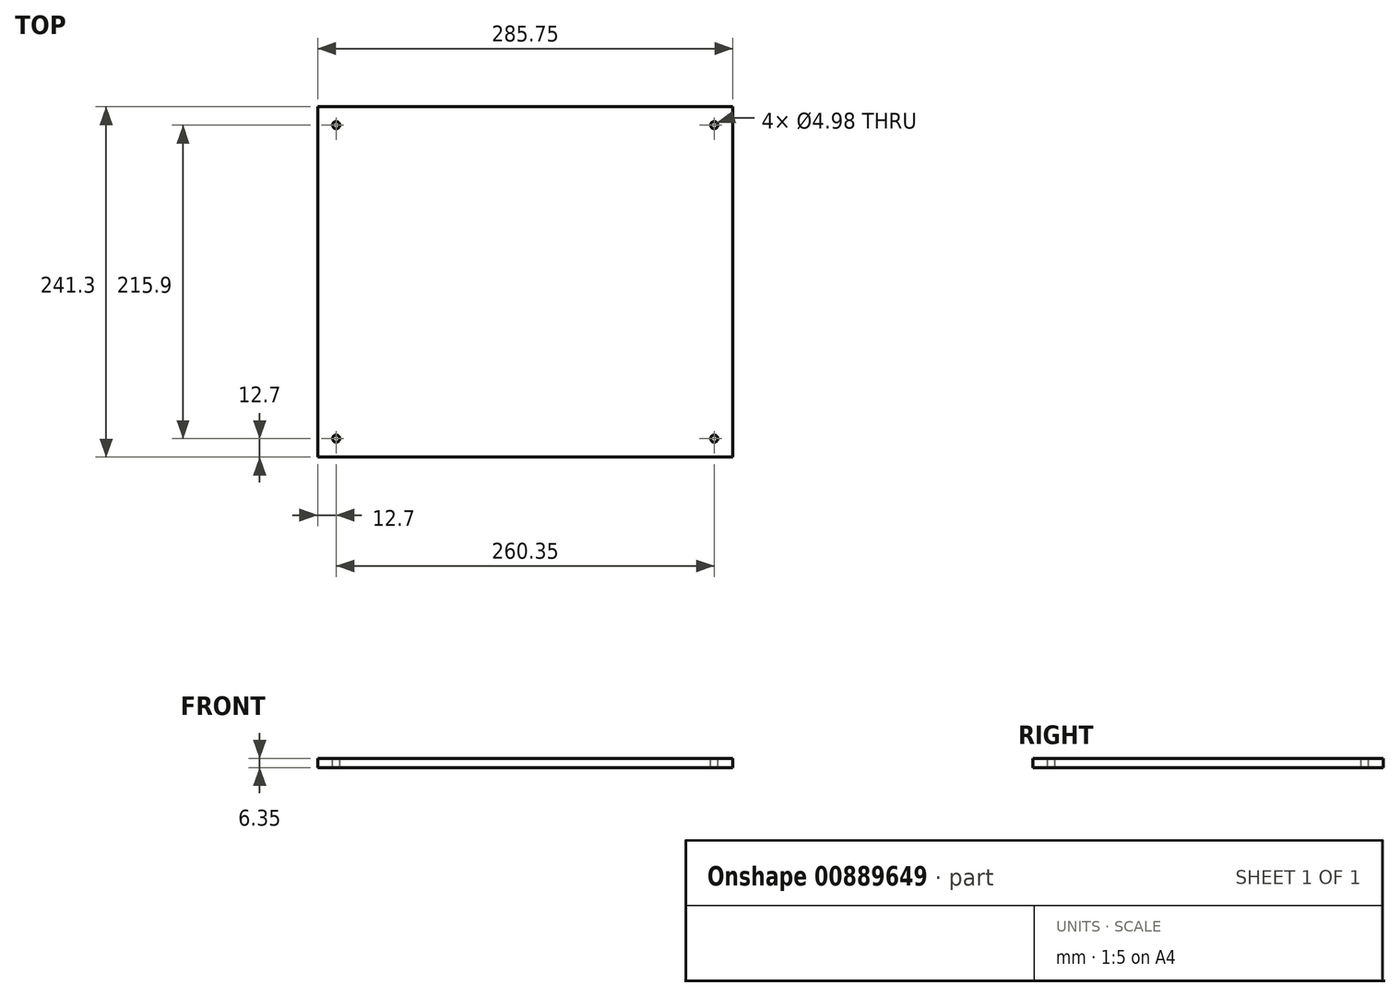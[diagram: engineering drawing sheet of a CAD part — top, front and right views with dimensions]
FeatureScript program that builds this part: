
annotation { "Feature Type Name" : "Feature", "Feature Type Description" : "" }
export const myFeature = defineFeature(function(context is Context, id is Id, definition is map)
    precondition{}
    {
        {
            var Q0;
            Q0=qCreatedBy(makeId("Top.planeOp"),FACE);
            var sketch = newSketch(context, id + "F0", { "sketchPlane" : qUnion([Q0])});
            skLineSegment(sketch, "E0.bottom", {"start": v(0, 0) * mm, "end": v(285.75, 0) * mm});
            skLineSegment(sketch, "E0.top", {"start": v(0, 241.3) * mm, "end": v(285.75, 241.3) * mm});
            skLineSegment(sketch, "E0.left", {"start": v(0, 0) * mm, "end": v(0, 241.3) * mm});
            skLineSegment(sketch, "E0.right", {"start": v(285.75, 0) * mm, "end": v(285.75, 241.3) * mm});
            skSolve(sketch);
        }
        {
            var Q0;
            Q0 = qSketchRegion(id + "F0", true);
            extrude(context, id + "F1", {"entities" : qUnion([Q0]), "depth" : 6.35 * mm, "offsetDistance" : 25.4 * mm});
        }
        {
            var Q0;
            Q0=makeQuery(id+"F1.opExtrude","CAP_FACE",FACE,{"disambiguationData":[OSD([sQuery(id+"F0.wireOp",EDGE,"E0.bottom"),sQuery(id+"F0.wireOp",EDGE,"E0.top"),sQuery(id+"F0.wireOp",EDGE,"E0.left"),sQuery(id+"F0.wireOp",EDGE,"E0.right")])],"isStart":false});
            var sketch = newSketch(context, id + "F2", { "sketchPlane" : qUnion([Q0])});
            skCircle(sketch, "E1", {"center": v(12.7, 12.7) * mm, "radius": 2.49 * mm});
            skCircle(sketch, "E2", {"center": v(12.7, 228.6) * mm, "radius": 2.49 * mm});
            skCircle(sketch, "E3", {"center": v(273.05, 228.6) * mm, "radius": 2.49 * mm});
            skCircle(sketch, "E4", {"center": v(273.05, 12.7) * mm, "radius": 2.49 * mm});
            skSolve(sketch);
        }
        {
            var Q0;
            Q0 = qSketchRegion(id + "F2", true);
            extrude(context, id + "F3", {"entities" : qUnion([Q0]), "operationType" : NewBodyOperationType.REMOVE, "oppositeDirection" : true, "depth" : 25.4 * mm, "offsetDistance" : 25.4 * mm});
        }
    });
